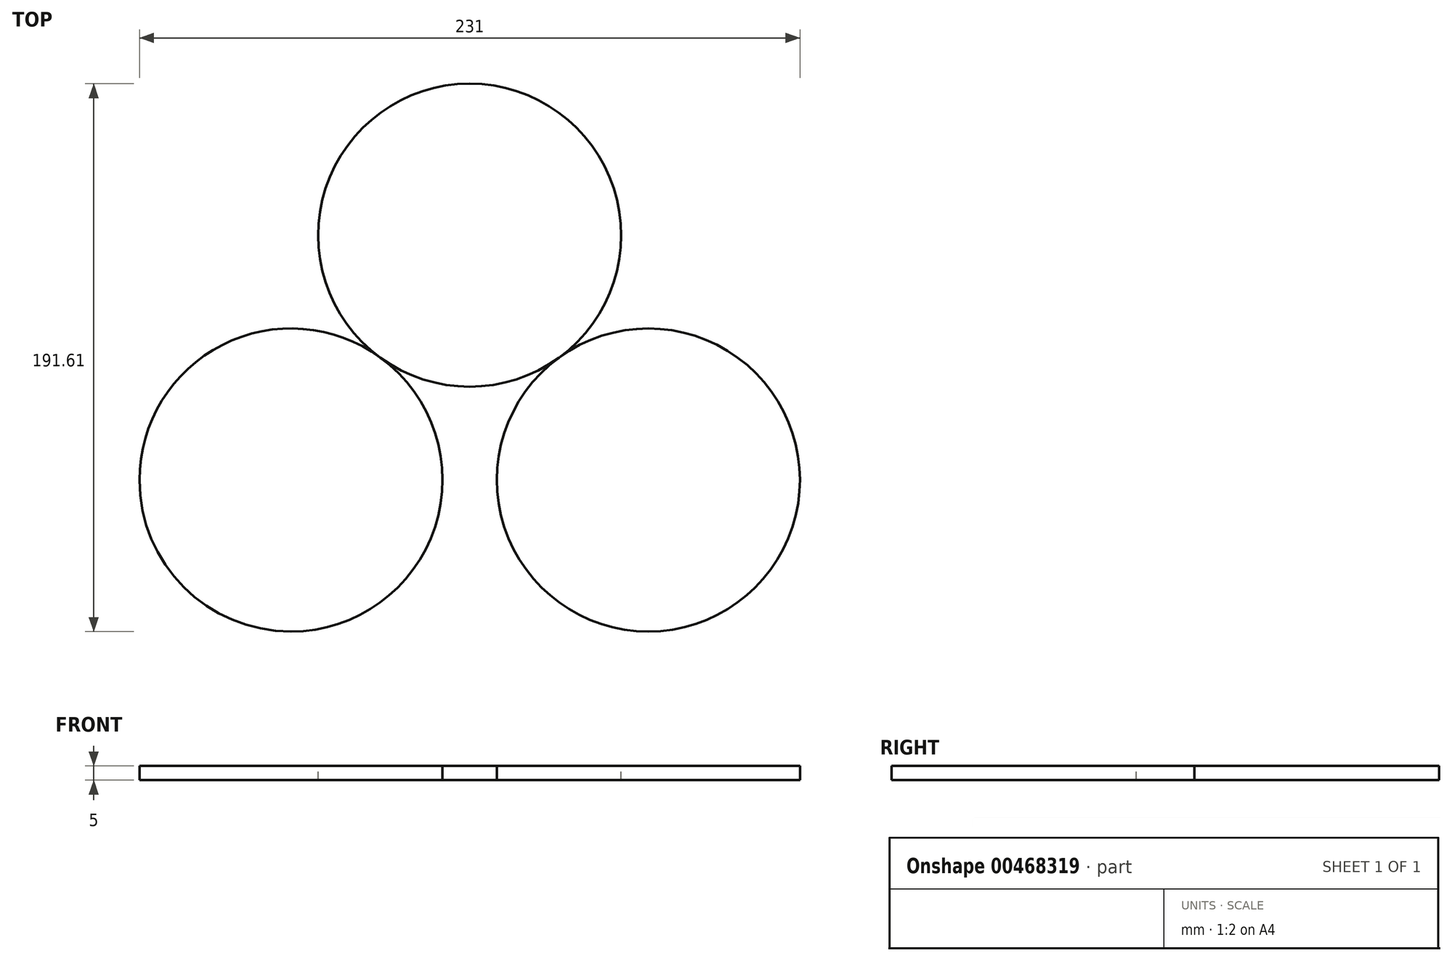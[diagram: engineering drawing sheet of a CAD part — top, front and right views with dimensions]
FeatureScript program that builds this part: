
annotation { "Feature Type Name" : "Feature", "Feature Type Description" : "" }
export const myFeature = defineFeature(function(context is Context, id is Id, definition is map)
    precondition{}
    {
        {
            var Q0;
            Q0=qCreatedBy(makeId("Top.planeOp"),FACE);
            var sketch = newSketch(context, id + "F0", { "sketchPlane" : qUnion([Q0])});
            skLineSegment(sketch, "E0.bottom", {"start": v(0, 0) * mm, "end": v(80, 0) * mm});
            skLineSegment(sketch, "E0.top", {"start": v(0, 80) * mm, "end": v(80, 80) * mm});
            skLineSegment(sketch, "E0.left", {"start": v(0, 0) * mm, "end": v(0, 80) * mm});
            skLineSegment(sketch, "E0.right", {"start": v(80, 0) * mm, "end": v(80, 80) * mm});
            skCircle(sketch, "E1", {"center": v(23.65, 56.47) * mm, "radius": 22.5 * mm});
            skCircle(sketch, "E2", {"center": v(55.95, 23.82) * mm, "radius": 22.5 * mm});
            skCircle(sketch, "E3", {"center": v(-414.84, 138.61) * mm, "radius": 53 * mm});
            skLineSegment(sketch, "E4.bottom", {"start": v(-49.34, 515) * mm, "end": v(-655.34, 515) * mm});
            skLineSegment(sketch, "E4.top", {"start": v(-49.34, 0) * mm, "end": v(-655.34, 0) * mm});
            skLineSegment(sketch, "E4.left", {"start": v(-49.34, 515) * mm, "end": v(-49.34, 0) * mm});
            skLineSegment(sketch, "E4.right", {"start": v(-655.34, 515) * mm, "end": v(-655.34, 0) * mm});
            skCircle(sketch, "E5", {"center": v(-539.84, 138.61) * mm, "radius": 53 * mm});
            skCircle(sketch, "E6", {"center": v(-602.34, 53) * mm, "radius": 53 * mm});
            skCircle(sketch, "E7", {"center": v(-102.34, 53) * mm, "radius": 53 * mm});
            skCircle(sketch, "E8", {"center": v(-227.34, 53) * mm, "radius": 53 * mm});
            skCircle(sketch, "E9", {"center": v(-352.34, 53) * mm, "radius": 53 * mm});
            skCircle(sketch, "E10", {"center": v(-477.34, 53) * mm, "radius": 53 * mm});
            skCircle(sketch, "E11", {"center": v(-289.84, 138.61) * mm, "radius": 53 * mm});
            skCircle(sketch, "E12", {"center": v(-164.84, 138.61) * mm, "radius": 53 * mm});
            skLineSegment(sketch, "E13", {"start": v(-602.34, 53) * mm, "end": v(-477.34, 53) * mm, "construction": true});
            skLineSegment(sketch, "E14", {"start": v(-352.34, 53) * mm, "end": v(-227.34, 53) * mm, "construction": true});
            skLineSegment(sketch, "E15", {"start": v(-227.34, 53) * mm, "end": v(-102.34, 53) * mm, "construction": true});
            skLineSegment(sketch, "E16", {"start": v(-477.34, 53) * mm, "end": v(-352.34, 53) * mm, "construction": true});
            skLineSegment(sketch, "E17", {"start": v(-539.84, 138.61) * mm, "end": v(-414.84, 138.61) * mm, "construction": true});
            skLineSegment(sketch, "E18", {"start": v(-289.84, 138.61) * mm, "end": v(-164.84, 138.61) * mm, "construction": true});
            skLineSegment(sketch, "E19", {"start": v(-414.84, 138.61) * mm, "end": v(-289.84, 138.61) * mm, "construction": true});
            skLineSegment(sketch, "E20", {"start": v(-539.84, 138.61) * mm, "end": v(-477.34, 53) * mm, "construction": true});
            skPoint(sketch, "E21", {"position": v(-508.6, 95.8) * mm});
            skLineSegment(sketch, "E22", {"start": v(-477.34, 53) * mm, "end": v(-414.84, 138.61) * mm, "construction": true});
            skSolve(sketch);
        }
        {
            var Q0;
            {var subQ0=sQuery(id+"F0.wireOp",EDGE,"E5");var subQ1=makeQuery(id+"F0.imprint","INTERSECT",VERTEX,{"derivedFrom":[subQ0,sQuery(id+"F0.wireOp",EDGE,"E6")]});Q0=makeQuery(id+"F0.imprint","IMPRINT",FACE,{"disambiguationData":[TD([[makeQuery(id+"F0.imprint","IMPRINT",EDGE,{"disambiguationData":[TD([[subQ1,-1.0]])],"derivedFrom":subQ0}),1.0]])]});}
            var Q1;
            {var subQ0=sQuery(id+"F0.wireOp",EDGE,"E6");var subQ1=makeQuery(id+"F0.imprint","INTERSECT",VERTEX,{"derivedFrom":[sQuery(id+"F0.wireOp",EDGE,"E4.right"),subQ0]});Q1=makeQuery(id+"F0.imprint","IMPRINT",FACE,{"disambiguationData":[TD([[makeQuery(id+"F0.imprint","IMPRINT",EDGE,{"disambiguationData":[TD([[subQ1,1.0]])],"derivedFrom":subQ0}),1.0]])]});}
            var Q2;
            {var subQ0=sQuery(id+"F0.wireOp",EDGE,"E10");var subQ1=makeQuery(id+"F0.imprint","INTERSECT",VERTEX,{"derivedFrom":[sQuery(id+"F0.wireOp",EDGE,"E3"),subQ0]});Q2=makeQuery(id+"F0.imprint","IMPRINT",FACE,{"disambiguationData":[TD([[makeQuery(id+"F0.imprint","IMPRINT",EDGE,{"disambiguationData":[TD([[subQ1,-1.0]])],"derivedFrom":subQ0}),1.0]])]});}
            extrude(context, id + "F1", {"entities" : qUnion([Q0, Q1, Q2]), "oppositeDirection" : true, "depth" : 5 * mm, "offsetDistance" : 25 * mm});
        }
    });
